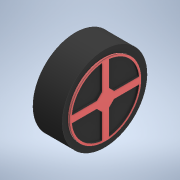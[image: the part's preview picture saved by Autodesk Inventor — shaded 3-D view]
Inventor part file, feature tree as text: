
AUTODESK INVENTOR PART (.ipt)
format: ipt  version: 2020 (Build 240168000, 168)  size: 177,152 bytes
history: native  units: in
note: dims shown in document units (in); Inventor stores cm internally (conversion verified against a paired STEP export)
features: sketch x5, extrude x4, hole x1
ambient origin geometry x8: Origin, YZ Plane, XZ Plane, XY Plane, X Axis, Y Axis, Z Axis, Center Point
bodies: Solid1 (feature_tree), Solid2 (feature_tree)
feature tree (10):
  extrude  "Extrusion1"  Depth=0.3937in TaperAngle=0.0deg
  sketch  "Sketch2"  dims[d3=1.0236in d4=0.3543in d5=0.0in]
  extrude  "Extrusion2"  Depth=0.3543in TaperAngle=0.0deg
  hole  "Hole1"  [1 undecoded]
  extrude  "Extrusion3"  Depth=0.2362in TaperAngle=360.0deg
  extrude  "Extrusion4"  TaperAngle=0.0deg  [1 undecoded]
  sketch  "Sketch1"  dims[d0=0.8661in d1=0.3937in d2=0.0in]
  sketch  "Sketch3"  dims[d6=0.0787in d7=0.2362in d8=0.1575in d9=0.0787in d10=90.0deg d11=0.315in d12=0.8108in d13=0.1181in]
  sketch  "Sketch4"  dims[d14=0.2362in d15=0.0in d16=1.5748in d18=360.0deg]
  sketch  "Sketch6"  dims[d20=1.5748in d22=360.0deg d24=0.0in d25=0.0in d17=0.0344in d26=0.0197in d27=0.0344in]
note: 2 required parameter values undecoded (feature->parameter linkage not recoverable at this tier; creation-order binding heuristic only, values carry confidence <= 0.55)
